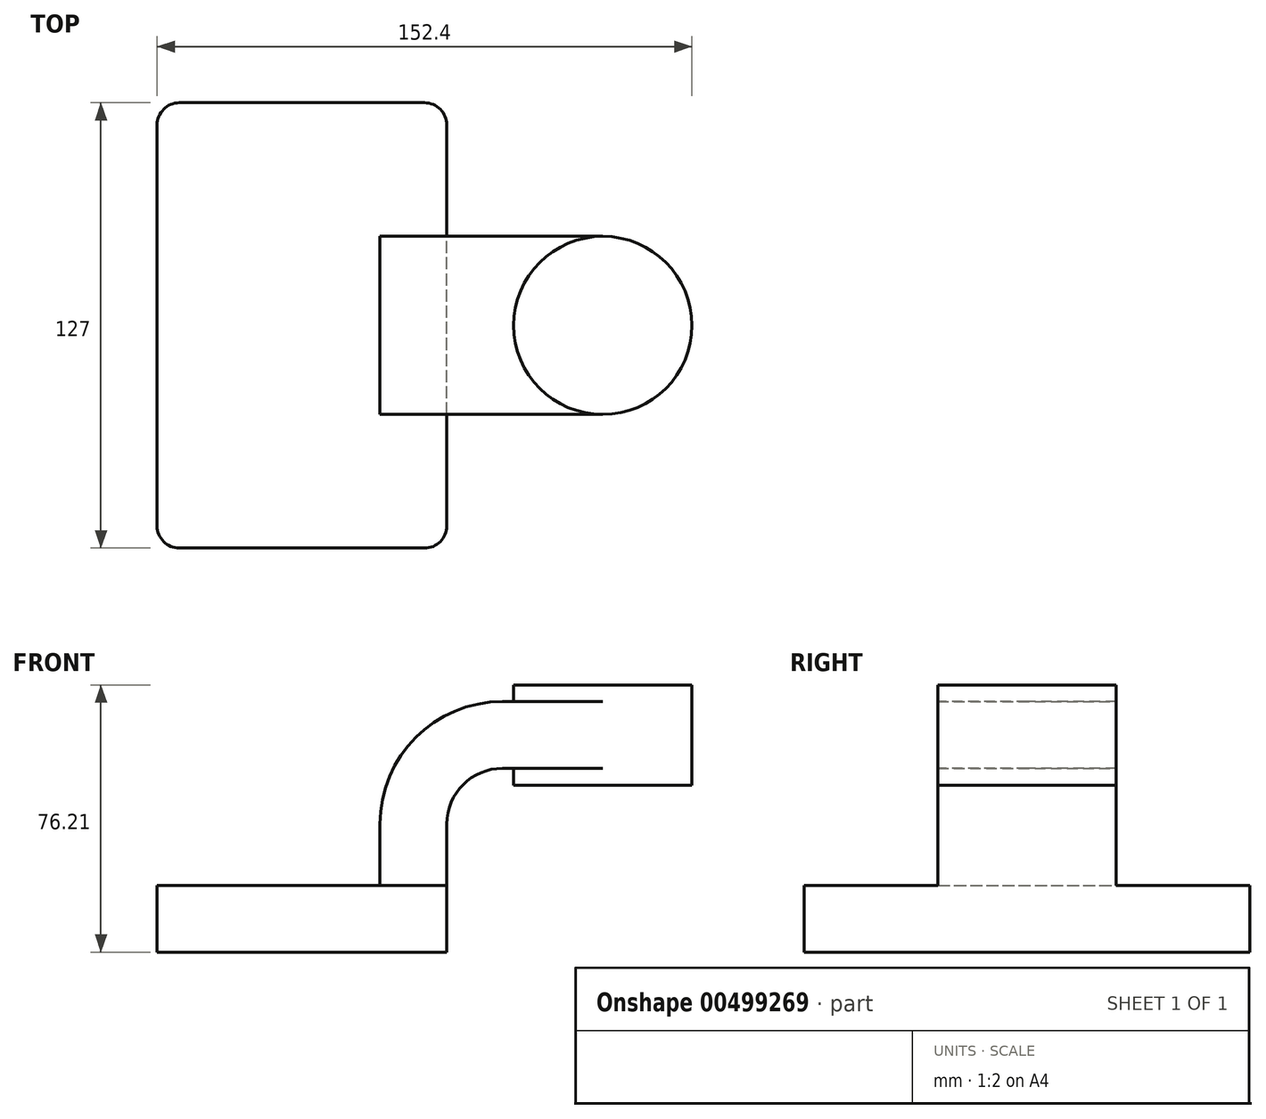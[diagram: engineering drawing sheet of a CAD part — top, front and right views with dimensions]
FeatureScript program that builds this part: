
annotation { "Feature Type Name" : "Feature", "Feature Type Description" : "" }
export const myFeature = defineFeature(function(context is Context, id is Id, definition is map)
    precondition{}
    {
        {
            var Q0;
            Q0=qCreatedBy(makeId("Front.planeOp"),FACE);
            var sketch = newSketch(context, id + "F0", { "sketchPlane" : qUnion([Q0])});
            skLineSegment(sketch, "E0.bottom", {"start": v(41.28, 9.53) * mm, "end": v(-41.28, 9.53) * mm});
            skLineSegment(sketch, "E0.top", {"start": v(41.28, -9.53) * mm, "end": v(-41.28, -9.53) * mm});
            skLineSegment(sketch, "E0.left", {"start": v(41.28, 9.53) * mm, "end": v(41.28, -9.53) * mm});
            skLineSegment(sketch, "E0.right", {"start": v(-41.28, 9.53) * mm, "end": v(-41.28, -9.53) * mm});
            skPoint(sketch, "E0.middle", {"position": v(0, 0) * mm});
            skLineSegment(sketch, "E1.bottom", {"start": v(111.12, 66.68) * mm, "end": v(60.32, 66.68) * mm});
            skLineSegment(sketch, "E1.top", {"start": v(111.12, 38.1) * mm, "end": v(60.32, 38.1) * mm});
            skLineSegment(sketch, "E1.left", {"start": v(111.12, 66.68) * mm, "end": v(111.12, 38.1) * mm});
            skLineSegment(sketch, "E1.right", {"start": v(60.32, 66.68) * mm, "end": v(60.32, 38.1) * mm});
            skPoint(sketch, "E1.middle", {"position": v(85.72, 52.39) * mm});
            skLineSegment(sketch, "E2", {"start": v(41.28, 9.53) * mm, "end": v(41.28, 27) * mm});
            skArc(sketch, "E3", {"start": v(41.27, 27) * mm, "mid": v(45.92, 38.23) * mm, "end": v(57.15, 42.88) * mm});
            skLineSegment(sketch, "E4", {"start": v(57.15, 42.88) * mm, "end": v(85.72, 42.88) * mm});
            skLineSegment(sketch, "E5.0", {"start": v(57.15, 61.93) * mm, "end": v(85.72, 61.93) * mm});
            skArc(sketch, "E5.1", {"start": v(22.22, 27) * mm, "mid": v(32.45, 51.7) * mm, "end": v(57.15, 61.93) * mm});
            skLineSegment(sketch, "E5.2", {"start": v(22.22, 9.53) * mm, "end": v(22.22, 27) * mm});
            skLineSegment(sketch, "E6", {"start": v(85.72, 38.1) * mm, "end": v(85.72, 66.68) * mm});
            skFitSpline(sketch, "E7", {"points": [v(-41.28, 9.53) * mm, v(57.15, 61.93) * mm], "startDerivative": vector(1.55, 121.33) * mm, "endDerivative": vector(120.73, -0.36) * mm});
            skSolve(sketch);
        }
        {
            var Q0;
            Q0=makeQuery(id+"F0.imprint","IMPRINT",FACE,{"disambiguationData":[TD([[makeQuery(id+"F0.imprint","IMPRINT",EDGE,{"derivedFrom":sQuery(id+"F0.wireOp",EDGE,"E0.top")}),-1.0]])]});
            extrude(context, id + "F1", {"entities" : qUnion([Q0]), "endBound" : BoundingType.SYMMETRIC, "depth" : 127 * mm, "offsetDistance" : 25.4 * mm});
        }
        {
            var Q0;
            {var subQ1=sQuery(id+"F0.wireOp",EDGE,"E2");Q0=makeQuery(id+"F0.imprint","IMPRINT",FACE,{"disambiguationData":[TD([[makeQuery(id+"F0.imprint","IMPRINT",EDGE,{"derivedFrom":subQ1}),1.0]])]});}
            var Q1;
            {var subQ0=sQuery(id+"F0.wireOp",EDGE,"E5.0");var subQ1=sQuery(id+"F0.wireOp",EDGE,"E1.right");var subQ2=makeQuery(id+"F0.imprint","INTERSECT",VERTEX,{"derivedFrom":[subQ1,subQ0]});Q1=makeQuery(id+"F0.imprint","IMPRINT",FACE,{"disambiguationData":[TD([[makeQuery(id+"F0.imprint","IMPRINT",EDGE,{"disambiguationData":[TD([[subQ2,-1.0]])],"derivedFrom":subQ1}),1.0]])]});}
            extrude(context, id + "F2", {"entities" : qUnion([Q0, Q1]), "operationType" : NewBodyOperationType.ADD, "endBound" : BoundingType.SYMMETRIC, "depth" : 50.8 * mm, "offsetDistance" : 25.4 * mm});
        }
        {
            var Q0;
            Q0=makeQuery(id+"F0.imprint","IMPRINT",FACE,{"disambiguationData":[TD([[makeQuery(id+"F0.imprint","IMPRINT",EDGE,{"derivedFrom":sQuery(id+"F0.wireOp",EDGE,"E5.1")}),1.0]])]});
            extrude(context, id + "F3", {"entities" : qUnion([Q0]), "operationType" : NewBodyOperationType.ADD, "endBound" : BoundingType.SYMMETRIC, "depth" : 15.88 * mm, "offsetDistance" : 25.4 * mm});
        }
        {
            var Q0;
            {var subQ4=sQuery(id+"F0.wireOp",EDGE,"E1.left");Q0=makeQuery(id+"F0.imprint","IMPRINT",FACE,{"disambiguationData":[TD([[makeQuery(id+"F0.imprint","IMPRINT",EDGE,{"derivedFrom":subQ4}),-1.0]])]});}
            var Q1;
            Q1=sQuery(id+"F0.wireOp",EDGE,"E6");
            revolve(context, id + "F4", {"operationType" : NewBodyOperationType.ADD, "entities" : qUnion([Q0]), "axis" : qUnion([Q1]), "revolveType" : RevolveType.FULL});
        }
        {
            var Q0;
            Q0=makeQuery(id+"F1.opExtrude","CAP_EDGE",EDGE,{"disambiguationData":[OSD([sQuery(id+"F0.wireOp",EDGE,"E0.left")])],"isStart":false});
            var Q1;
            Q1=makeQuery(id+"F1.opExtrude","CAP_EDGE",EDGE,{"disambiguationData":[OSD([sQuery(id+"F0.wireOp",EDGE,"E0.left")])],"isStart":true});
            var Q2;
            Q2=makeQuery(id+"F1.opExtrude","CAP_EDGE",EDGE,{"disambiguationData":[OSD([sQuery(id+"F0.wireOp",EDGE,"E0.right")])],"isStart":true});
            var Q3;
            Q3=makeQuery(id+"F1.opExtrude","CAP_EDGE",EDGE,{"disambiguationData":[OSD([sQuery(id+"F0.wireOp",EDGE,"E0.right")])],"isStart":false});
            fillet(context, id + "F5", {"entities" : qUnion([Q0, Q1, Q2, Q3]), "radius" : 6.35 * mm, "tangentPropagation" : true, "allowEdgeOverflow" : false});
        }
    });
